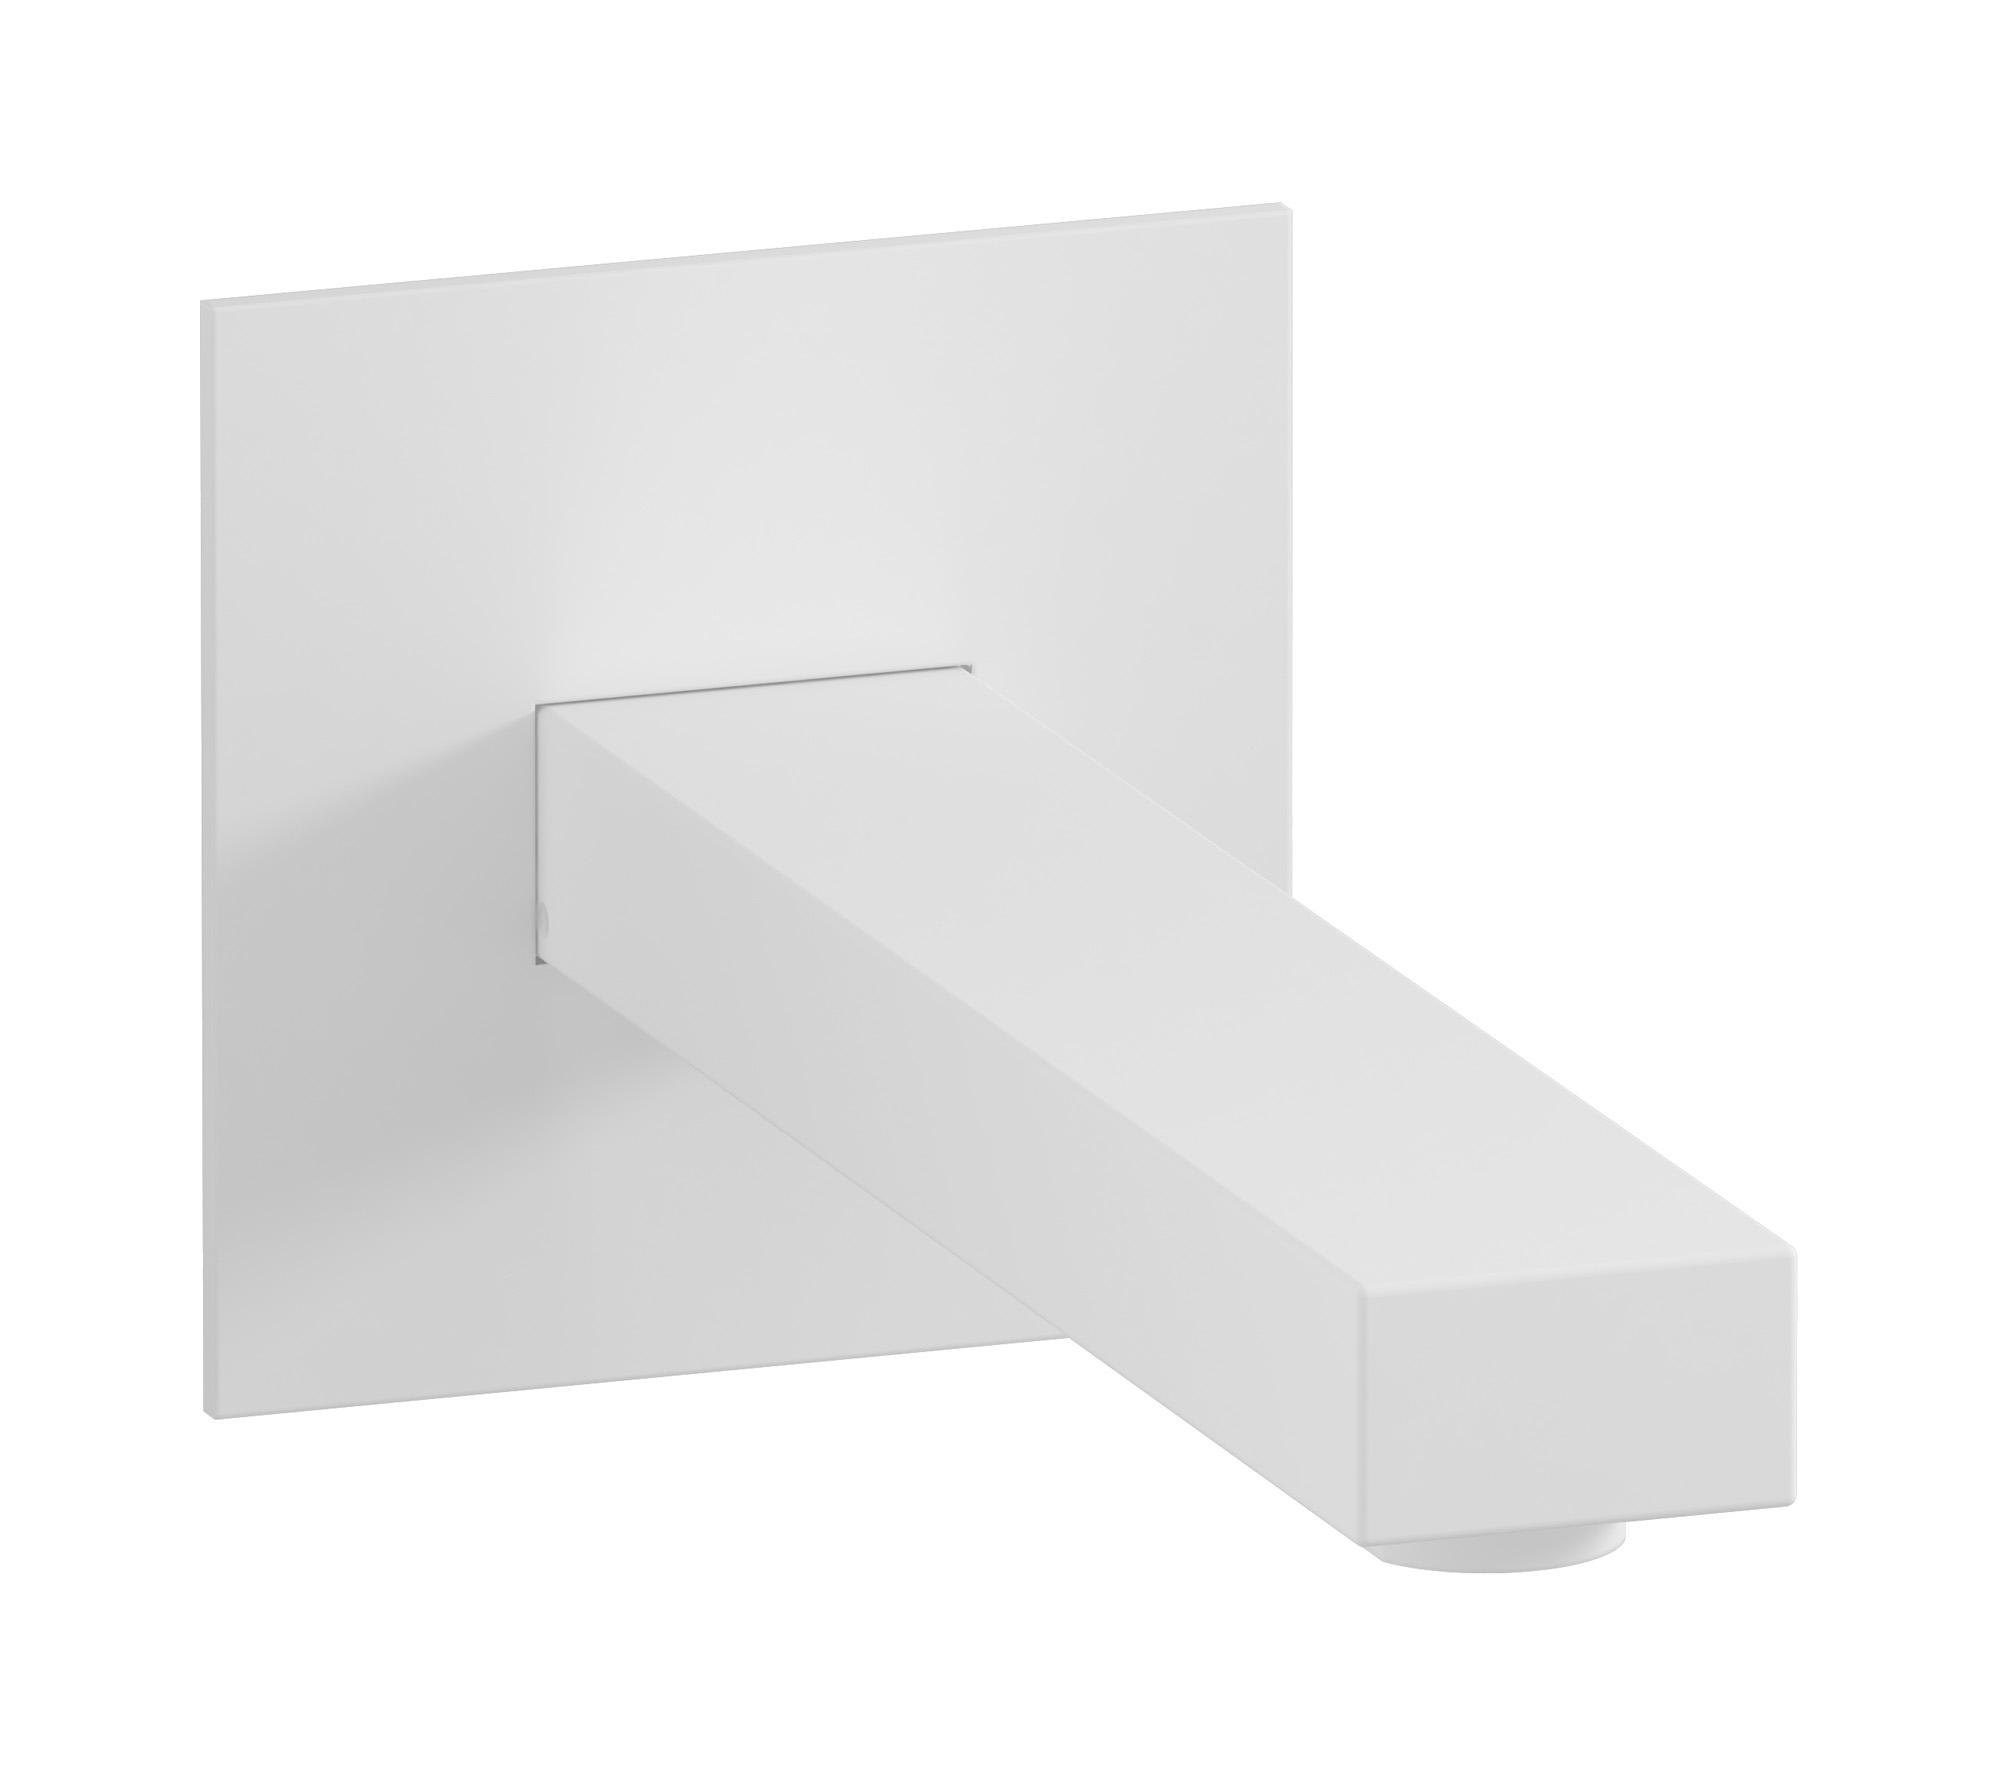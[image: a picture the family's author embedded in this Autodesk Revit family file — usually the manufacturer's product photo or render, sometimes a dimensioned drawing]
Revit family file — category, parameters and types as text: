
# Revit family: RU320
name_source: partatom
category: Apparecchi idraulici
units: mm (PartAtom-declared; Revit-internal decimal feet)

## family parameters
Basato su piano di lavoro = No
Condiviso = No
Mantieni orientamento annotazione = No
Numero OmniClass = 23.45.55.17
Punto di calcolo locali = No
Quota connettore circolare = Usa diametro
Sempre verticale = Sì
Taglio con vuoti quando caricato = No
Tipo di parte = Normale
Titolo OmniClass = Mixing Faucets

## types (12) — shared parameters
Commenti sul tipo = Wall mounted spout
Connessione CW = No
Connessione HW = No
Connessione di scarico = No
Connessione di ventilazione = No
Descrizione = Wall mounted spout
Produttore = IB Rubinetterie S.p.A.
URL = https://www.weareib.it
Water inlet = 10 mm  [stored 0.0328084 ft]
zero-valued in all types: Prospetto di default

## per-type parameters (varying)
| type | Finishes surface | Immagine tipo | Modello |
| Chrome | IB_Chrome | RU320CC.jpg | RU320CC |
| Matt White | IB_matt white | RU320BO.jpg | RU320BO |
| Black Chrome | IB_Black chrome | RU320CF.jpg | RU320CF |
| Brushed Black Chrome | IB_Brushed black chrome | RU320CS.jpg | RU320CS |
| Pale Gold | IB_Pale gold | RU320II.jpg | RU320II |
| Brushed Pale Gold | IB_brushed pale gold | RU320IS.jpg | RU320IS |
| Matt Black | IB_matt black | RU320NP.jpg | RU320NP |
| Gold | IB_gold | RU320OO.jpg | RU320OO |
| Brushed Gold | IB_brushed gold | RU320OS.jpg | RU320OS |
| Rose Gold | IB_Rose gold | RU320RS.jpg | RU320RS |
| Brushed Rose Gold | IB_Brushed rose gold | RU320SR.jpg | RU320SR |
| Brushed Nickel | IB_Brushed nickel | RU320SS.jpg | RU320SS |

note: [stored X ft] marks values corroborated as IEEE doubles in the binary element streams (Revit-internal decimal feet)
